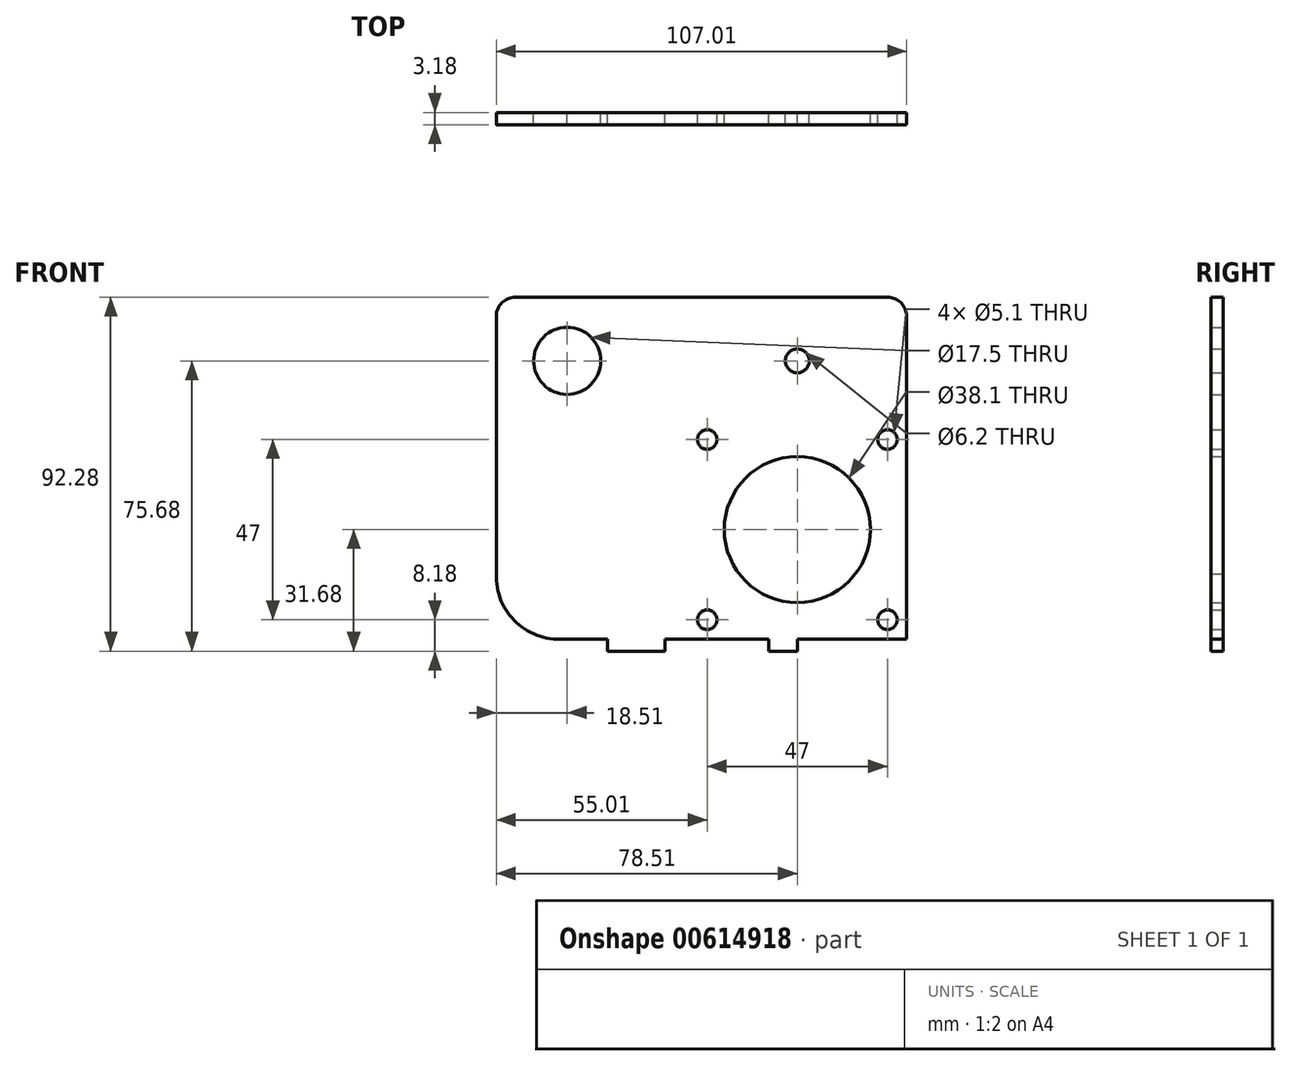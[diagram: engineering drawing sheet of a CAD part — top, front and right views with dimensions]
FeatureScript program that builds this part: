
annotation { "Feature Type Name" : "Feature", "Feature Type Description" : "" }
export const myFeature = defineFeature(function(context is Context, id is Id, definition is map)
    precondition{}
    {
        {
            var Q0;
            Q0=qCreatedBy(makeId("Front.planeOp"),FACE);
            var sketch = newSketch(context, id + "F0", { "sketchPlane" : qUnion([Q0])});
            skLineSegment(sketch, "E0.bottom", {"start": v(-28.5, 28.5) * mm, "end": v(23.5, 28.5) * mm});
            skLineSegment(sketch, "E0.top", {"start": v(-28.5, -28.5) * mm, "end": v(28.5, -28.5) * mm});
            skLineSegment(sketch, "E0.left", {"start": v(-28.5, 28.5) * mm, "end": v(-28.5, -28.5) * mm});
            skLineSegment(sketch, "E0.right", {"start": v(28.5, 23.5) * mm, "end": v(28.5, -28.5) * mm});
            skPoint(sketch, "E0.middle", {"position": v(0, 0) * mm});
            skLineSegment(sketch, "E1.bottom", {"start": v(28.5, -28.5) * mm, "end": v(13.5, -28.5) * mm});
            skLineSegment(sketch, "E1.top", {"start": v(28.5, -31.68) * mm, "end": v(13.5, -31.68) * mm});
            skLineSegment(sketch, "E1.left", {"start": v(28.5, -28.5) * mm, "end": v(28.5, -31.68) * mm});
            skLineSegment(sketch, "E1.right", {"start": v(13.5, -28.5) * mm, "end": v(13.5, -31.67) * mm});
            skLineSegment(sketch, "E2.bottom", {"start": v(-28.5, -28.5) * mm, "end": v(-13.5, -28.5) * mm});
            skLineSegment(sketch, "E2.top", {"start": v(-28.5, -31.67) * mm, "end": v(-13.5, -31.67) * mm});
            skLineSegment(sketch, "E2.left", {"start": v(-28.5, -28.5) * mm, "end": v(-28.5, -31.67) * mm});
            skLineSegment(sketch, "E2.right", {"start": v(-13.5, -28.5) * mm, "end": v(-13.5, -31.67) * mm});
            skLineSegment(sketch, "E3.bottom", {"start": v(0, -28.5) * mm, "end": v(7.5, -28.5) * mm});
            skLineSegment(sketch, "E3.top", {"start": v(0, -31.67) * mm, "end": v(7.5, -31.67) * mm});
            skLineSegment(sketch, "E3.left", {"start": v(0, -28.5) * mm, "end": v(0, -31.67) * mm});
            skLineSegment(sketch, "E3.right", {"start": v(7.5, -28.5) * mm, "end": v(7.5, -31.67) * mm});
            skLineSegment(sketch, "E4.bottom", {"start": v(0, -31.67) * mm, "end": v(-7.5, -31.67) * mm});
            skLineSegment(sketch, "E4.top", {"start": v(0, -28.5) * mm, "end": v(-7.5, -28.5) * mm});
            skLineSegment(sketch, "E4.left", {"start": v(0, -31.67) * mm, "end": v(0, -28.5) * mm});
            skLineSegment(sketch, "E4.right", {"start": v(-7.5, -31.67) * mm, "end": v(-7.5, -28.5) * mm});
            skCircle(sketch, "E5", {"center": v(0, 0) * mm, "radius": 19.05 * mm});
            skLineSegment(sketch, "E6.bottom", {"start": v(-23.5, 23.5) * mm, "end": v(23.5, 23.5) * mm});
            skLineSegment(sketch, "E6.top", {"start": v(-23.5, -23.5) * mm, "end": v(23.5, -23.5) * mm});
            skLineSegment(sketch, "E6.left", {"start": v(-23.5, 23.5) * mm, "end": v(-23.5, -23.5) * mm});
            skLineSegment(sketch, "E6.right", {"start": v(23.5, 23.5) * mm, "end": v(23.5, -23.5) * mm});
            skCircle(sketch, "E7", {"center": v(23.5, 23.5) * mm, "radius": 2.55 * mm});
            skCircle(sketch, "E8.MirrorC", {"center": v(-23.5, 23.5) * mm, "radius": 2.55 * mm});
            skCircle(sketch, "E9.MirrorC", {"center": v(-23.5, -23.5) * mm, "radius": 2.55 * mm});
            skCircle(sketch, "E10.MirrorC", {"center": v(23.5, -23.5) * mm, "radius": 2.55 * mm});
            skPoint(sketch, "E11.visualSharp", {"position": v(28.5, 28.5) * mm});
            skPoint(sketch, "E12.visualSharp", {"position": v(23.5, 28.5) * mm});
            skLineSegment(sketch, "E12.filletArc", {"start": v(23.5, 28.5) * mm, "end": v(23.5, 28.5) * mm});
            skLineSegment(sketch, "E13", {"start": v(23.5, 28.5) * mm, "end": v(28.5, 28.5) * mm});
            skLineSegment(sketch, "E14", {"start": v(28.5, 23.5) * mm, "end": v(28.5, 28.5) * mm});
            skCircle(sketch, "E15", {"center": v(-60, 44) * mm, "radius": 8.75 * mm});
            skPoint(sketch, "E16.visualSharp", {"position": v(-78.5, 28.5) * mm});
            skLineSegment(sketch, "E17", {"start": v(-28.5, -28.5) * mm, "end": v(-34.5, -28.5) * mm});
            skLineSegment(sketch, "E18", {"start": v(-34.5, -28.5) * mm, "end": v(-49.5, -28.5) * mm});
            skLineSegment(sketch, "E19", {"start": v(-49.5, -28.5) * mm, "end": v(-49.5, -31.68) * mm});
            skLineSegment(sketch, "E20", {"start": v(-49.5, -31.67) * mm, "end": v(-34.5, -31.67) * mm});
            skLineSegment(sketch, "E21", {"start": v(-34.5, -31.68) * mm, "end": v(-34.5, -28.5) * mm});
            skLineSegment(sketch, "E22", {"start": v(0, 0) * mm, "end": v(0, 44) * mm});
            skCircle(sketch, "E23", {"center": v(0, 44) * mm, "radius": 3.1 * mm});
            skLineSegment(sketch, "E24.bottom", {"start": v(-28.5, 28.5) * mm, "end": v(28.5, 28.5) * mm});
            skLineSegment(sketch, "E24.top", {"start": v(-28.5, 60.6) * mm, "end": v(23.5, 60.6) * mm});
            skLineSegment(sketch, "E24.left", {"start": v(-28.5, 28.5) * mm, "end": v(-28.5, 60.6) * mm});
            skLineSegment(sketch, "E24.right", {"start": v(28.5, 28.5) * mm, "end": v(28.5, 55.6) * mm});
            skLineSegment(sketch, "E25", {"start": v(-60, 44) * mm, "end": v(-60, -28.5) * mm});
            skLineSegment(sketch, "E26", {"start": v(-60, 44) * mm, "end": v(0, 44) * mm});
            skLineSegment(sketch, "E27", {"start": v(0, 44) * mm, "end": v(0, 44) * mm});
            skLineSegment(sketch, "E28", {"start": v(-28.5, 60.6) * mm, "end": v(-73.5, 60.6) * mm});
            skLineSegment(sketch, "E29", {"start": v(-78.5, 55.6) * mm, "end": v(-78.5, -11.5) * mm});
            skPoint(sketch, "E30.visualSharp", {"position": v(-78.5, 60.6) * mm});
            skArc(sketch, "E30.filletArc", {"start": v(-73.5, 60.6) * mm, "mid": v(-77.04, 59.13) * mm, "end": v(-78.5, 55.6) * mm});
            skArc(sketch, "E31", {"start": v(-78.5, -11.5) * mm, "mid": v(-73.2, -24.29) * mm, "end": v(-60, -28.5) * mm});
            skLineSegment(sketch, "E32", {"start": v(-60, -28.5) * mm, "end": v(-49.5, -28.5) * mm});
            skPoint(sketch, "E33.visualSharp", {"position": v(28.5, 60.6) * mm});
            skArc(sketch, "E33.filletArc", {"start": v(28.5, 55.6) * mm, "mid": v(27.04, 59.13) * mm, "end": v(23.5, 60.6) * mm});
            skSolve(sketch);
        }
        {
            var Q0;
            Q0=makeQuery(id+"F0.imprint","IMPRINT",FACE,{"disambiguationData":[TD([[makeQuery(id+"F0.imprint","IMPRINT",EDGE,{"derivedFrom":sQuery(id+"F0.wireOp",EDGE,"E5")}),-1.0]])]});
            var Q1;
            Q1=makeQuery(id+"F0.imprint","IMPRINT",FACE,{"disambiguationData":[TD([[makeQuery(id+"F0.imprint","IMPRINT",EDGE,{"derivedFrom":sQuery(id+"F0.wireOp",EDGE,"E1.bottom")}),1.0]])]});
            var Q2;
            Q2=makeQuery(id+"F0.imprint","IMPRINT",FACE,{"disambiguationData":[TD([[makeQuery(id+"F0.imprint","IMPRINT",EDGE,{"derivedFrom":sQuery(id+"F0.wireOp",EDGE,"E3.bottom")}),-1.0]])]});
            var Q3;
            Q3=makeQuery(id+"F0.imprint","IMPRINT",FACE,{"disambiguationData":[TD([[makeQuery(id+"F0.imprint","IMPRINT",EDGE,{"derivedFrom":sQuery(id+"F0.wireOp",EDGE,"E4.bottom")}),-1.0]])]});
            var Q4;
            Q4=makeQuery(id+"F0.imprint","IMPRINT",FACE,{"disambiguationData":[TD([[makeQuery(id+"F0.imprint","IMPRINT",EDGE,{"derivedFrom":sQuery(id+"F0.wireOp",EDGE,"E2.bottom")}),-1.0]])]});
            var Q5;
            Q5=makeQuery(id+"F0.imprint","IMPRINT",FACE,{"disambiguationData":[TD([[makeQuery(id+"F0.imprint","IMPRINT",EDGE,{"derivedFrom":sQuery(id+"F0.wireOp",EDGE,"E0.bottom")}),-1.0]])]});
            var Q6;
            Q6=makeQuery(id+"F0.imprint","IMPRINT",FACE,{"disambiguationData":[TD([[makeQuery(id+"F0.imprint","IMPRINT",EDGE,{"derivedFrom":sQuery(id+"F0.wireOp",EDGE,"E15")}),-1.0]])]});
            var Q7;
            Q7=makeQuery(id+"F0.imprint","IMPRINT",FACE,{"disambiguationData":[TD([[makeQuery(id+"F0.imprint","IMPRINT",EDGE,{"derivedFrom":sQuery(id+"F0.wireOp",EDGE,"E18")}),1.0]])]});
            var Q8;
            {var subQ10=sQuery(id+"F0.wireOp",EDGE,"UBpU5qTn-KrrS-G8ys-hke9-8aA7W8N4lxMn");var subQ11=sQuery(id+"F0.wireOp",EDGE,"E5");var subQ12=makeQuery(id+"F0.imprint","INTERSECT",VERTEX,{"derivedFrom":[subQ11,subQ10]});Q8=makeQuery(id+"F0.imprint","IMPRINT",FACE,{"disambiguationData":[TD([[makeQuery(id+"F0.imprint","IMPRINT",EDGE,{"disambiguationData":[TD([[subQ12,-1.0]])],"derivedFrom":subQ11}),-1.0]])]});}
            var Q9;
            Q9=makeQuery(id+"F0.imprint","IMPRINT",FACE,{"disambiguationData":[TD([[makeQuery(id+"F0.imprint","IMPRINT",EDGE,{"derivedFrom":sQuery(id+"F0.wireOp",EDGE,"E0.right")}),-1.0]])]});
            var Q10;
            {var subQ5=sQuery(id+"F0.wireOp",EDGE,"E8.MirrorC");var subQ6=sQuery(id+"F0.wireOp",EDGE,"E6.bottom");var subQ7=makeQuery(id+"F0.imprint","INTERSECT",VERTEX,{"derivedFrom":[subQ6,subQ5]});Q10=makeQuery(id+"F0.imprint","IMPRINT",FACE,{"disambiguationData":[TD([[makeQuery(id+"F0.imprint","IMPRINT",EDGE,{"disambiguationData":[TD([[subQ7,-1.0]])],"derivedFrom":subQ6}),1.0]])]});}
            var Q11;
            Q11=makeQuery(id+"F0.imprint","IMPRINT",FACE,{"disambiguationData":[TD([[makeQuery(id+"F0.imprint","IMPRINT",EDGE,{"derivedFrom":sQuery(id+"F0.wireOp",EDGE,"E23")}),-1.0]])]});
            var Q12;
            {var subQ0=sQuery(id+"F0.wireOp",EDGE,"E24.top");Q12=makeQuery(id+"F0.imprint","IMPRINT",FACE,{"disambiguationData":[TD([[makeQuery(id+"F0.imprint","IMPRINT",EDGE,{"derivedFrom":subQ0}),-1.0]])]});}
            extrude(context, id + "F1", {"entities" : qUnion([Q0, Q1, Q2, Q3, Q4, Q5, Q6, Q7, Q8, Q9, Q10, Q11, Q12]), "depth" : 3.17 * mm, "offsetDistance" : 25 * mm});
        }
    });
